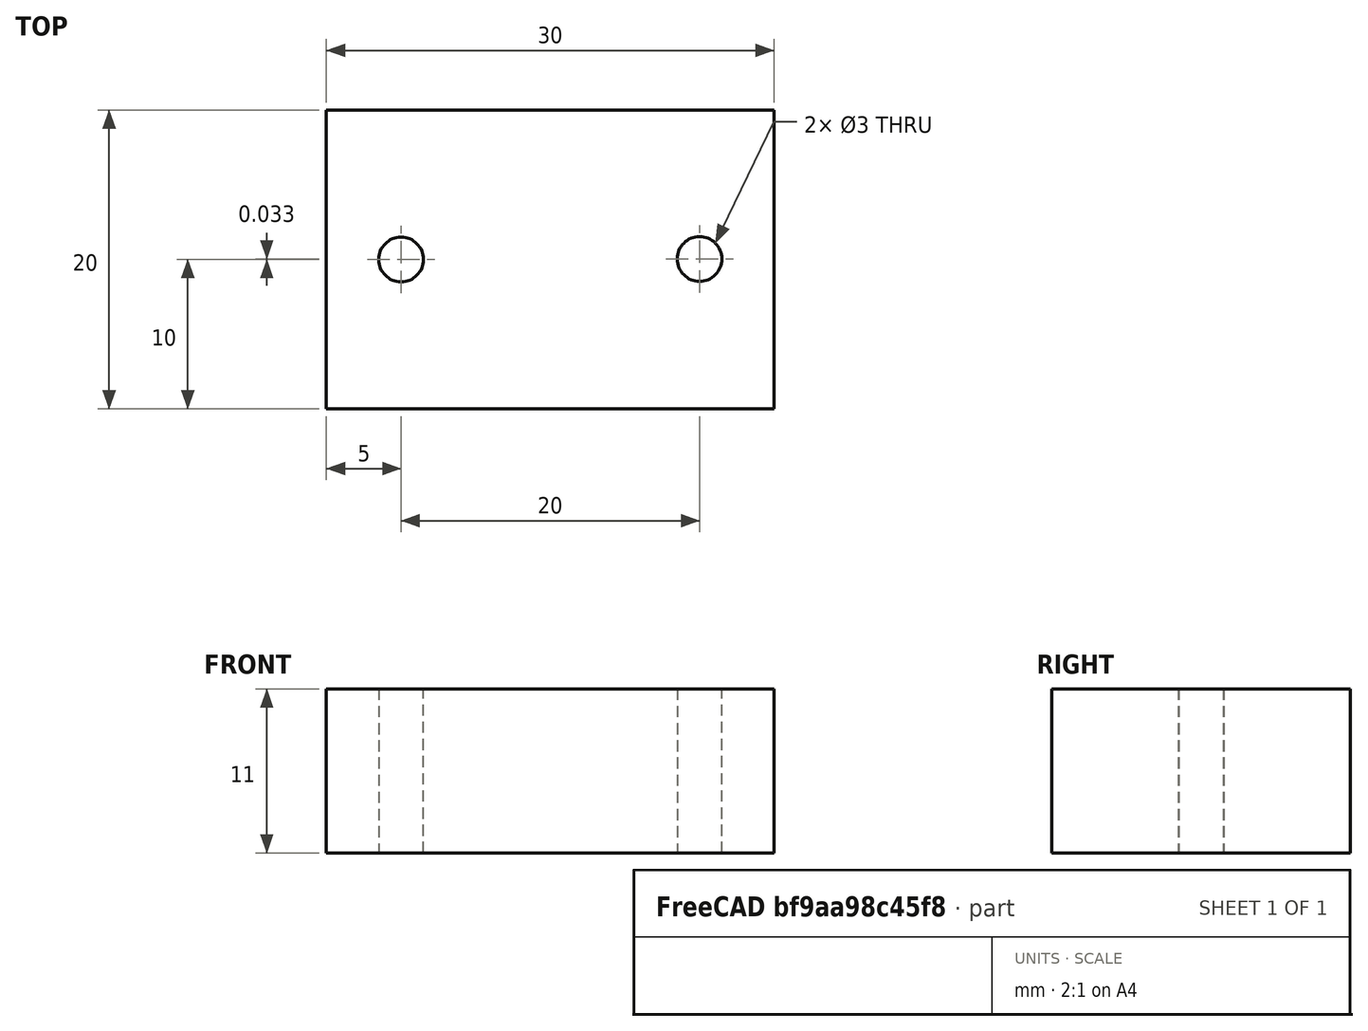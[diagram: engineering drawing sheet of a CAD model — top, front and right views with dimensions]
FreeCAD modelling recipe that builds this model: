
FCSTD DOCUMENT  (FreeCAD 0.16R6707 (Git))
Label: butée_fc_vertical
License: All rights reserved
LicenseURL: http://en.wikipedia.org/wiki/All_rights_reserved
objects: Sketcher::SketchObject×1, PartDesign::Pad×1
note: 3 computed .brp shape members not serialized (recipe doc carries the construction recipe); baked Part::Feature solids carry a one-line shape summary decoded from their .brp

FEATURE [Sketcher::SketchObject] Sketch
  sketch-geometry (6):
    g0: LineSegment StartX=0 StartY=0 StartZ=0 EndX=30 EndY=0 EndZ=0
    g1: LineSegment StartX=30 StartY=0 StartZ=0 EndX=30 EndY=20 EndZ=0
    g2: LineSegment StartX=30 StartY=20 StartZ=0 EndX=0 EndY=20 EndZ=0
    g3: LineSegment StartX=0 StartY=20 StartZ=0 EndX=0 EndY=0 EndZ=0
    g4: Circle CenterX=5 CenterY=10 CenterZ=0 NormalX=0 NormalY=0 NormalZ=1 Radius=1.5
    g5: Circle CenterX=25 CenterY=10.0334 CenterZ=0 NormalX=0 NormalY=0 NormalZ=1 Radius=1.5
  constraints (16):
    c: Coincident(g0,g1)
    c: Coincident(g1,g2)
    c: Coincident(g2,g3)
    c: Coincident(g3,g0)
    c: Horizontal(g0)
    c: Horizontal(g2)
    c: Vertical(g1)
    c: Vertical(g3)
    c: Coincident(g0,g-1)
    c: Distance(g3) = 20
    c: Distance(g2) = 30
    c: Radius(g5) = 1.5
    c: Equal(g5,g4)
    c: DistanceX(g4,g5) = 20
    c: DistanceX(g2,g4) = 5
    c: DistanceY(g4) = 10
FEATURE [PartDesign::Pad] Pad
  Length = 11
  Length2 = 100
  Sketch = -> Sketch
  Type = 0
